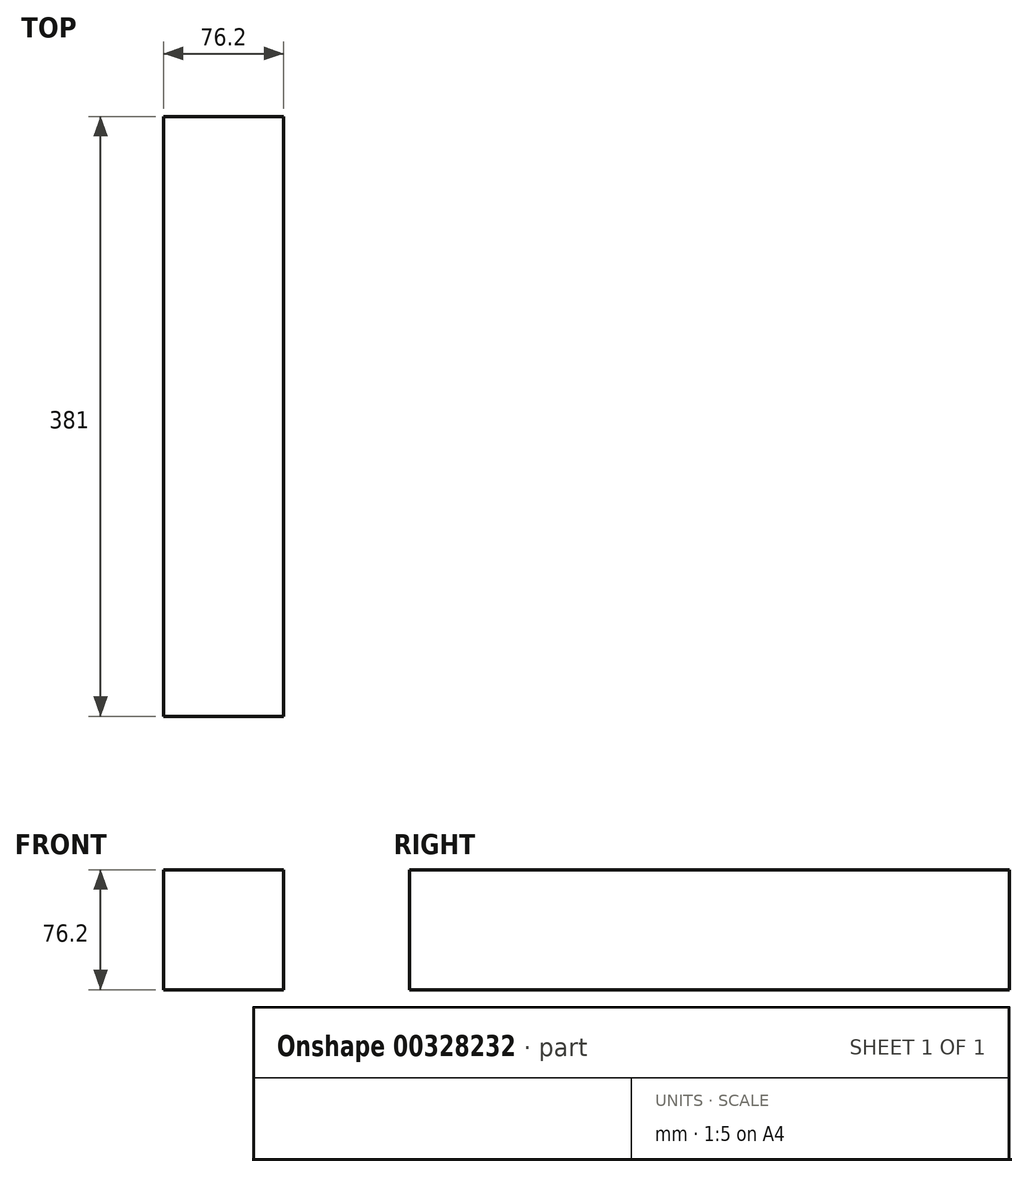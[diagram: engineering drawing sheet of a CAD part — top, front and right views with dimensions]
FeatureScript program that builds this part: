
annotation { "Feature Type Name" : "Feature", "Feature Type Description" : "" }
export const myFeature = defineFeature(function(context is Context, id is Id, definition is map)
    precondition{}
    {
        {
            var Q0;
            Q0=qCreatedBy(makeId("Front.planeOp"),FACE);
            var sketch = newSketch(context, id + "F0", { "sketchPlane" : qUnion([Q0])});
            skLineSegment(sketch, "E0", {"start": v(0, 0) * mm, "end": v(0, 76.2) * mm});
            skLineSegment(sketch, "E1", {"start": v(0, 76.2) * mm, "end": v(-76.2, 76.2) * mm});
            skLineSegment(sketch, "E2", {"start": v(-76.2, 76.2) * mm, "end": v(-76.2, 0) * mm});
            skLineSegment(sketch, "E3", {"start": v(-76.2, 0) * mm, "end": v(0, 0) * mm});
            skSolve(sketch);
        }
        {
            var Q0;
            Q0 = qSketchRegion(id + "F0", true);
            extrude(context, id + "F1", {"entities" : qUnion([Q0]), "depth" : 381 * mm});
        }
    });
